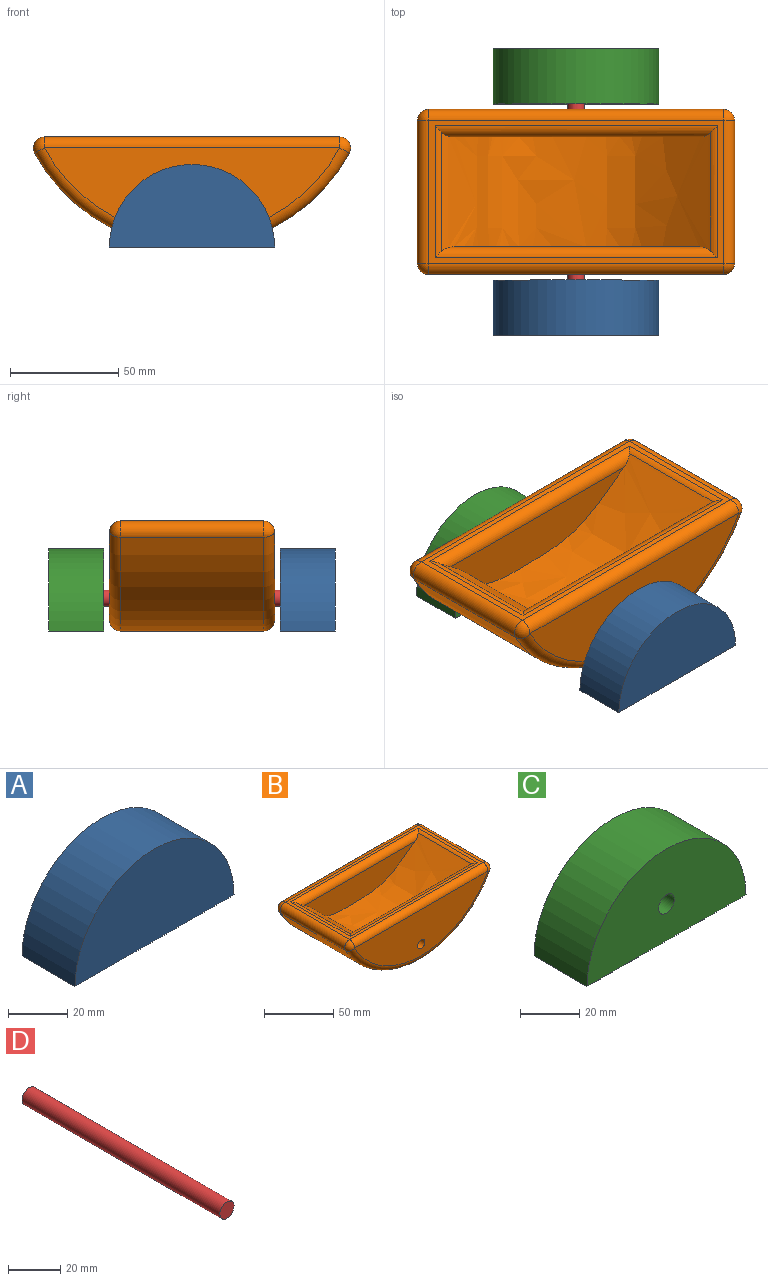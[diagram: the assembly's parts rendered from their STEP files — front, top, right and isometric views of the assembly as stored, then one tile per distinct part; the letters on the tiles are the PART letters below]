
ASSEMBLY  parts=4 mates=3
PART A: 6 faces, bbox 76.2x25.4x38.1 mm
  f0: cylinder r=38.1mm len=76.2mm, axis (0,1,0), area 3040.2mm2, adj f1,f2,f3
  f1: plane 76.2x25.4mm, normal (0,0,-1), area 1935.5mm2, adj f0,f2,f3
  f2: plane 76.2x38.1mm, normal (0,-1,0), area 2280.2mm2, adj f0,f1
  f3: plane 76.2x38.1mm, normal (0,1,0), area 2234.6mm2, adj f0,f1,f4
  f4: cylinder r=3.81mm len=12.7mm, axis (0,1,0), area 304mm2, adj f3,f5
  f5: plane 7.62x7.62mm, normal (0,1,0), area 45.6mm2, adj f4
PART B: 22 faces, bbox 157.2x76.2x57.6 mm
  f0: plane 136.31x66.04mm, normal (0,0,1), area 1057.8mm2, adj f7,f8,f9,f10,f11,f12,f13,f14
  f1: cylinder r=82.55mm len=145.25mm, axis (0,-1,0), area 11724.9mm2, adj f11,f14,f16,f19
  f2: plane 136.31x40.64mm, normal (0,1,0), area 3898.2mm2, adj f12,f16,f21
  f3: plane 136.31x40.64mm, normal (0,-1,0), area 3898.2mm2, adj f13,f19,f21
  f4: extruded ~124.32x55.21mm, area 7218.6mm2, adj f5,f6,f7,f8,f9,f10
  f5: plane 114.69x25.08mm, normal (0,-1,0), area 1914.8mm2, adj f4,f8
  f6: plane 114.69x25.08mm, normal (0,1,0), area 1914.8mm2, adj f4,f9
  f7: cylinder r=5.08mm len=60.96mm, axis (0,-1,0), area 193.9mm2, adj f0,f4,f8,f9
  f8: cylinder r=5.08mm len=130.32mm, axis (-1,0,0), area 976.8mm2, adj f0,f4,f5,f7,f10
  f9: cylinder r=5.08mm len=130.32mm, axis (1,0,0), area 976.8mm2, adj f0,f4,f6,f7,f10
  f10: cylinder r=5.08mm len=60.96mm, axis (0,-1,0), area 177.2mm2, adj f0,f4,f8,f9
  f11: cylinder r=5.08mm len=66.04mm, axis (0,-1,0), area 693.2mm2, adj f0,f1,f15,f18
  f12: cylinder r=5.08mm len=136.31mm, axis (1,0,0), area 1087.7mm2, adj f0,f2,f15,f17
  f13: cylinder r=5.08mm len=136.31mm, axis (-1,0,0), area 1087.7mm2, adj f0,f3,f18,f20
  f14: cylinder r=5.08mm len=66.04mm, axis (0,-1,0), area 693.2mm2, adj f0,f1,f17,f20
  f15: sphere r=5.08mm, area 53.3mm2, adj f11,f12,f16
  f16: torus R=77.47mm, axis (0,-1,0), area 1385mm2, adj f1,f2,f15,f17
  f17: sphere r=5.08mm, area 53.3mm2, adj f12,f14,f16
  f18: sphere r=5.08mm, area 53.3mm2, adj f11,f13,f19
  f19: torus R=77.47mm, axis (0,-1,0), area 1385mm2, adj f1,f3,f18,f20
  f20: sphere r=5.08mm, area 53.3mm2, adj f13,f14,f19
  f21: cylinder r=3.81mm len=76.2mm, axis (0,-1,0), area 1824.1mm2, adj f2,f3
PART C: 6 faces, bbox 76.2x25.4x38.1 mm
  f0: plane 76.2x25.4mm, normal (0,0,-1), area 1935.5mm2, adj f1,f2,f3
  f1: cylinder r=38.1mm len=76.2mm, axis (0,1,0), area 3040.2mm2, adj f0,f2,f3
  f2: plane 76.2x38.1mm, normal (0,-1,0), area 2234.6mm2, adj f0,f1,f4
  f3: plane 76.2x38.1mm, normal (0,1,0), area 2280.2mm2, adj f0,f1
  f4: cylinder r=3.81mm len=12.7mm, axis (0,-1,0), area 304mm2, adj f2,f5
  f5: plane 7.62x7.62mm, normal (0,-1,0), area 45.6mm2, adj f4
PART D: 3 faces, bbox 7.6x106.7x7.6 mm
  f0: cylinder r=3.81mm len=106.68mm, axis (0,1,0), area 2553.8mm2, adj f1,f2
  f1: plane 7.62x7.62mm, normal (0,-1,0), area 45.6mm2, adj f0
  f2: plane 7.62x7.62mm, normal (0,1,0), area 45.6mm2, adj f0
PLACE A t=(-28.74,-51.15,12.72)mm
PLACE B t=(-28.74,-48.61,12.72)mm
PLACE C t=(-28.74,55.53,12.72)mm
PLACE D t=(-28.74,42.83,27.96)mm
MATE revolute C.f4 <-> D.f0  axis (0,-1,0) through (-28.74,42.83,27.96)mm
MATE revolute D.f0 <-> B.f21  axis (0,1,0) through (-28.74,-10.51,27.96)mm
MATE revolute A.f4 <-> D.f0  axis (0,1,0) through (-28.74,-63.85,27.96)mm
